# Revit family: WSL_A3-Skylight-Pyramid-SMARTBIM
name_source: partatom
category: Windows
revit_build: Autodesk Revit 2016 (Build: 20150220_1215(x64)
units: mm (PartAtom-declared; Revit-internal decimal feet)

## family parameters
Always vertical = No
Cut with Voids When Loaded = No
Host = Roof
Room Calculation Point = No
Shared = No

## types (1)
- Parametric
    04 CSI = 08 60 00
    95 CSI = 08600
    Assembly Code = B3020110
    Cap Height = 0' - 2"
    Cap Length = 0' - 3"
    Curb Depth = 0' - 3 1/2"
    Curb Height = 0' - 5"
    Frame = Metal Aluminium
    Frame Height = 0' - 3 1/2"
    Glass = skylight glass
    Glass Length = 3' - 1"
    Glass Width = 5' - 1"
    Height = 2' - 0"
    Length = 3' - 0"
    Manufacturer = SMARTBIM
    Mullion = Mullion Material
    Mullion Radius = 0' - 0 1/4"
    Mullion Radius Note = Only 1 inch
    SmartBIM Object Version = 3
    Subcategory = Skylight
    Total Frame Height = 0' - 8 1/2"
    Width = 5' - 0"

## geometry (parser evidence)
native form markers: Extrusion x4, Sweep x3
no freeform markers — native parametric forms only
